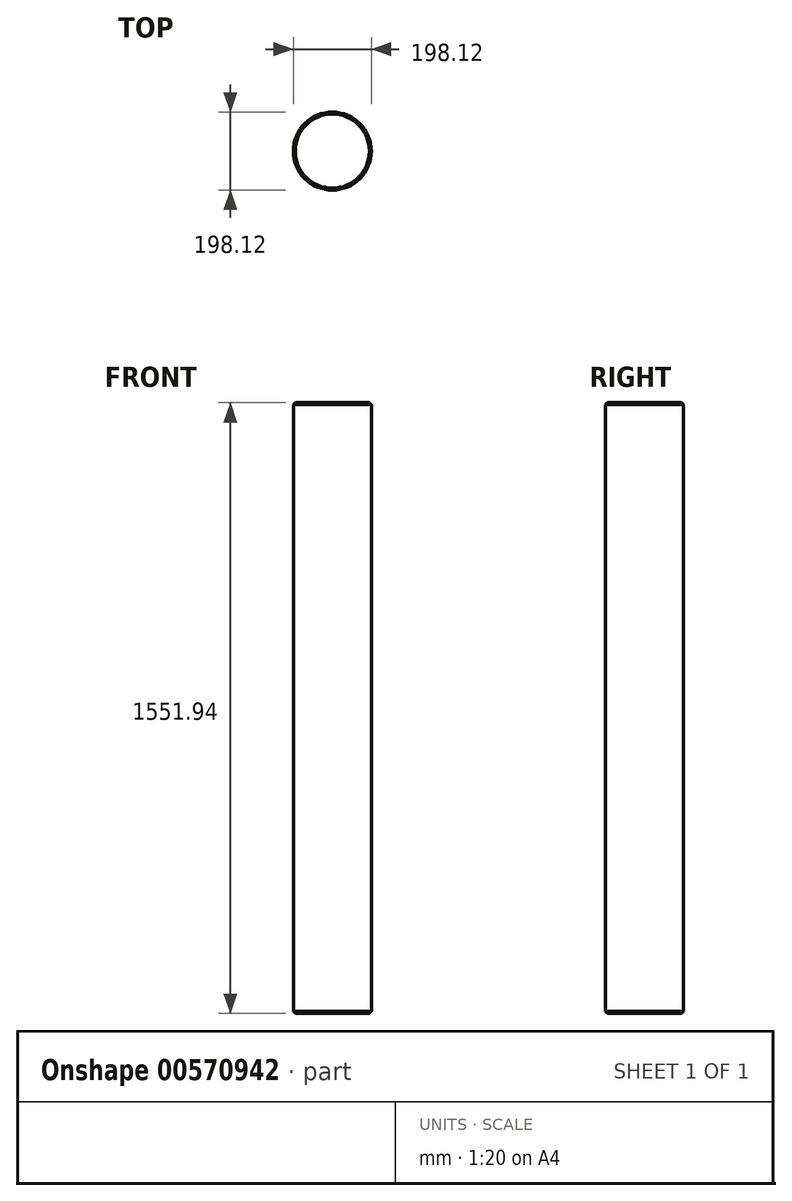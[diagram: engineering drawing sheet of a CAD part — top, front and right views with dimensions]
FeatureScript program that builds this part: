
annotation { "Feature Type Name" : "Feature", "Feature Type Description" : "" }
export const myFeature = defineFeature(function(context is Context, id is Id, definition is map)
    precondition{}
    {
        {
            var Q0;
            Q0=qCreatedBy(makeId("Top.planeOp"),FACE);
            var sketch = newSketch(context, id + "F0", { "sketchPlane" : qUnion([Q0])});
            skCircle(sketch, "E0", {"center": v(0, 0) * mm, "radius": 99.06 * mm});
            skSolve(sketch);
        }
        {
            var Q0;
            Q0 = qSketchRegion(id + "F0", true);
            extrude(context, id + "F1", {"entities" : qUnion([Q0]), "depth" : 309.88 * mm, "offsetDistance" : 25.4 * mm});
        }
        {
            var Q0;
            Q0=makeQuery(id+"F1.opExtrude","CAP_FACE",FACE,{"disambiguationData":[OSD([sQuery(id+"F0.wireOp",EDGE,"E0")])],"isStart":true});
            extrude(context, id + "F2", {"entities" : qUnion([Q0]), "operationType" : NewBodyOperationType.ADD, "depth" : 1242.06 * mm, "offsetDistance" : 25.4 * mm});
        }
        {
            var Q0;
            Q0=makeQuery(id+"F2.opExtrude","CAP_EDGE",EDGE,{"disambiguationData":[OSD([sQuery(id+"F0.wireOp",EDGE,"E0")])],"isStart":false});
            chamfer(context, id + "F3", {"entities" : qUnion([Q0]), "width" : 5.08 * mm, "tangentPropagation" : true});
        }
        {
            var Q0;
            Q0=makeQuery(id+"F1.opExtrude","CAP_EDGE",EDGE,{"disambiguationData":[OSD([sQuery(id+"F0.wireOp",EDGE,"E0")])],"isStart":false});
            chamfer(context, id + "F4", {"entities" : qUnion([Q0]), "width" : 5.08 * mm, "tangentPropagation" : true});
        }
    });
